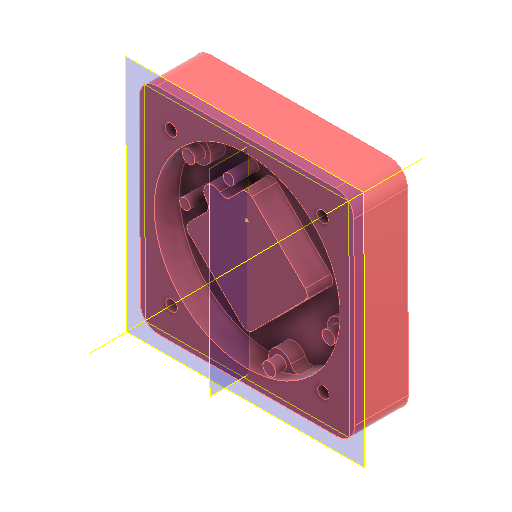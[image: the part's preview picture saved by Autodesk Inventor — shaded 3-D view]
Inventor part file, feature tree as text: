
AUTODESK INVENTOR PART (.ipt)
format: ipt  version: 2022 (Build 260153000, 153)  size: 484,864 bytes
history: native  units: mm
features: sketch x6, other x5, plane x4, extrude x2, fillet x2, projected_geometry x2, hole x1, imported_body x1, revolve x1, pattern_circular x1, reference x1
ambient origin geometry x8: Origin, YZ Plane, XZ Plane, XY Plane, X Axis, Y Axis, Z Axis, Center Point
bodies: Volumenkörper1 (feature_tree), Volumenkörper3 (feature_tree), Volumenkörper4 (feature_tree), Volumenkörper5 (feature_tree)
feature tree (26):
  plane  "Arbeitsebene1"
  extrude  "Extrusion1"  Depth=60.0mm
  fillet  "Rundung1"  Radius=5.0mm
  hole  "Bohrung1"  [1 undecoded]
  imported_body  "Basis2"
  other  "Kombinieren1"
  plane  "Arbeitsebene2"
  other  "Trennen1"
  extrude  "Extrusion3"  Depth=10.0mm
  plane  "Arbeitsebene3"
  plane  "Arbeitsebene4"
  revolve  "Umdrehung1"
  pattern_circular  "Runde Anordnung2"  [2 undecoded]
  fillet  "Rundung7"  Radius=12.5mm
  sketch  "Skizze8"  dims[d20=0.0mm d21=0.349066mm d23=-30.0mm d32=12.5mm d34=2.0mm d35=0.8mm d36=360.0deg d38=40.0mm d39=360.0deg d41=0.5mm d42=0.0mm]
  sketch  "Skizze1"  dims[d0=60.0mm d1=60.0mm]
  reference  "Referenz1"
  sketch  "Skizze2"  dims[d2=10.0mm d3=15.0mm d4=0.0mm d5=0.0mm d6=5.0mm]
  projected_geometry  "Projizierte Kontur1"
  sketch  "Skizze4"  dims[d7=60.0mm]
  sketch  "Skizze5"  dims[d8=3.2mm d9=6.0mm d10=6.5mm d11=4.0mm d12=90.0deg d13=8.0mm d14=20.594885mm d17=-15.5mm]
  sketch  "Skizze7"  dims[d18=10.0mm d19=4.0mm]
  projected_geometry  "Projizierte Kontur2"
  other  "IM_Mold_plate_top.ipt.iam"
  other  "IM_Matchboxscope_plate:1"
  other  "Baugruppe1"
note: 3 required parameter values undecoded (feature->parameter linkage not recoverable at this tier; creation-order binding heuristic only, values carry confidence <= 0.55)
